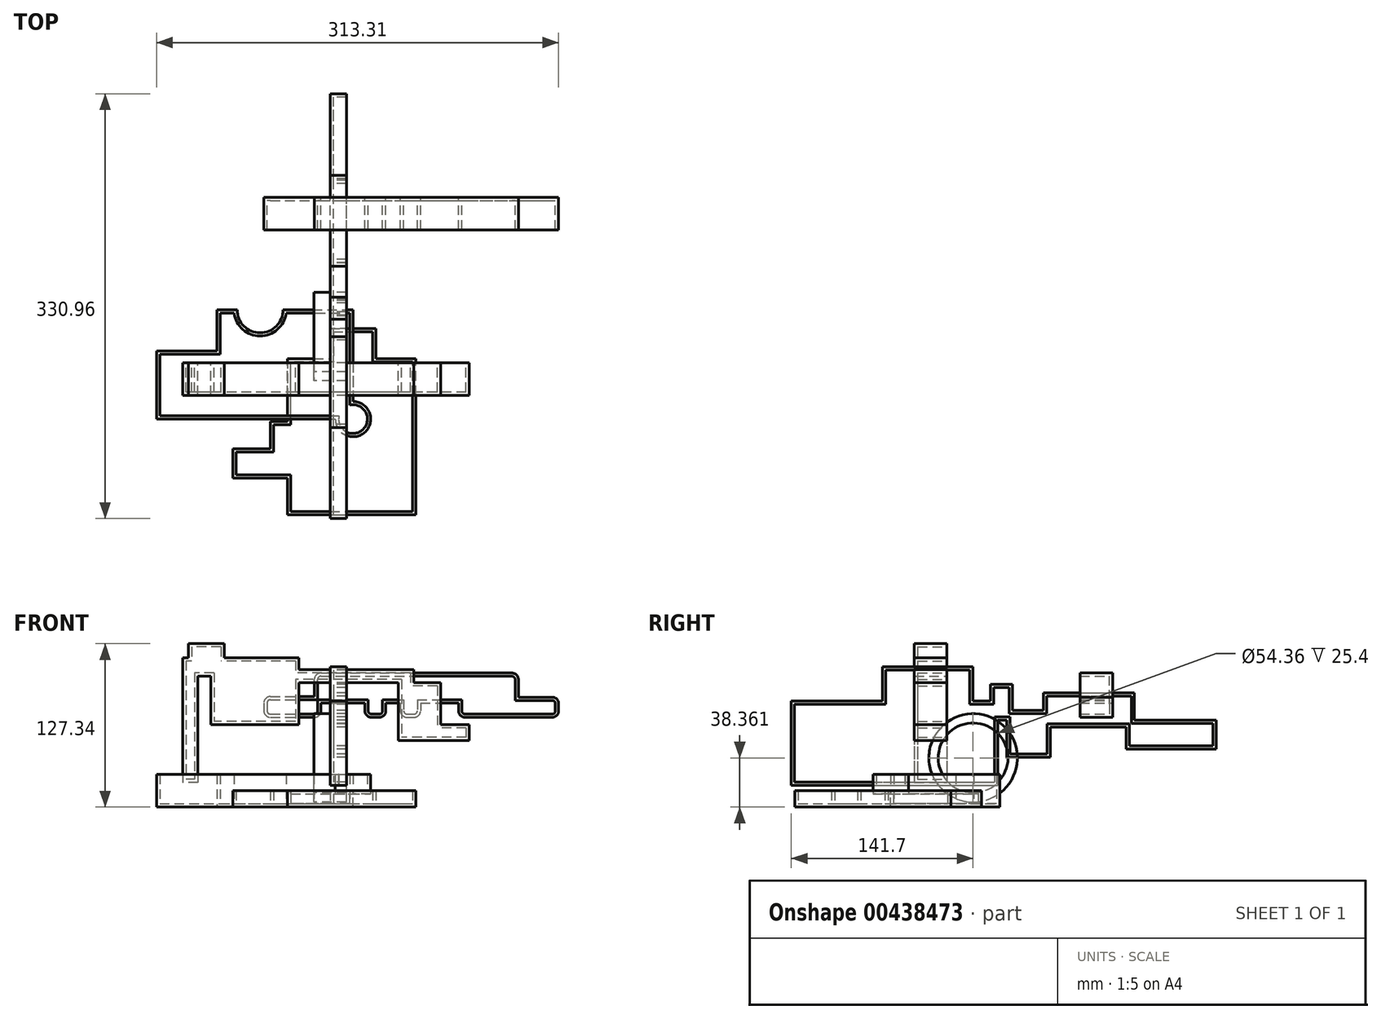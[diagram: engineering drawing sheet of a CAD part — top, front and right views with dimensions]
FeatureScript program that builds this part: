
annotation { "Feature Type Name" : "Feature", "Feature Type Description" : "" }
export const myFeature = defineFeature(function(context is Context, id is Id, definition is map)
    precondition{}
    {
        {
            var Q0;
            Q0=qCreatedBy(makeId("Top.planeOp"),FACE);
            var sketch = newSketch(context, id + "F0", { "sketchPlane" : qUnion([Q0])});
            skLineSegment(sketch, "E0.bottom", {"start": v(-135.25, -11) * mm, "end": v(17.85, -11) * mm});
            skLineSegment(sketch, "E0.top", {"start": v(-135.25, -64.2) * mm, "end": v(17.85, -64.2) * mm});
            skLineSegment(sketch, "E0.left", {"start": v(-135.25, -11) * mm, "end": v(-135.25, -64.2) * mm});
            skLineSegment(sketch, "E0.right", {"start": v(17.85, -11) * mm, "end": v(17.85, -64.2) * mm});
            skLineSegment(sketch, "E1.bottom", {"start": v(-88.25, -11) * mm, "end": v(17.85, -11) * mm});
            skLineSegment(sketch, "E1.top", {"start": v(-88.25, 20.9) * mm, "end": v(17.85, 20.9) * mm});
            skLineSegment(sketch, "E1.left", {"start": v(-88.25, -11) * mm, "end": v(-88.25, 20.9) * mm});
            skLineSegment(sketch, "E1.right", {"start": v(17.85, -11) * mm, "end": v(17.85, 20.9) * mm});
            skCircle(sketch, "E2", {"center": v(-54.53, 20.9) * mm, "radius": 17.86 * mm});
            skCircle(sketch, "E3", {"center": v(17.85, -64.2) * mm, "radius": 13.77 * mm});
            skSolve(sketch);
        }
        {
            var Q0;
            {var subQ0=sQuery(id+"F0.wireOp",EDGE,"E0.right");var subQ1=sQuery(id+"F0.wireOp",EDGE,"E0.top");var subQ2=makeQuery(id+"F0.imprint","INTERSECT",VERTEX,{"derivedFrom":[subQ1,subQ0]});Q0=makeQuery(id+"F0.imprint","IMPRINT",FACE,{"disambiguationData":[TD([[makeQuery(id+"F0.imprint","IMPRINT",EDGE,{"disambiguationData":[TD([[subQ2,1.0]])],"derivedFrom":subQ1}),-1.0]])]});}
            var Q1;
            {var subQ0=sQuery(id+"F0.wireOp",EDGE,"E2");var subQ1=sQuery(id+"F0.wireOp",EDGE,"E1.top");var subQ2=makeQuery(id+"F0.imprint","INTERSECT",VERTEX,{"disambiguationData":[OD(0.0)],"derivedFrom":[subQ1,subQ0]});Q1=makeQuery(id+"F0.imprint","IMPRINT",FACE,{"disambiguationData":[TD([[makeQuery(id+"F0.imprint","IMPRINT",EDGE,{"disambiguationData":[TD([[subQ2,-1.0]])],"derivedFrom":subQ1}),1.0]])]});}
            var Q2;
            {var subQ0=sQuery(id+"F0.wireOp",EDGE,"E0.right");var subQ1=sQuery(id+"F0.wireOp",EDGE,"E0.top");var subQ2=makeQuery(id+"F0.imprint","INTERSECT",VERTEX,{"derivedFrom":[subQ1,subQ0]});Q2=makeQuery(id+"F0.imprint","IMPRINT",FACE,{"disambiguationData":[TD([[makeQuery(id+"F0.imprint","IMPRINT",EDGE,{"disambiguationData":[TD([[subQ2,1.0]])],"derivedFrom":subQ1}),1.0]])]});}
            var Q3;
            Q3=makeQuery(id+"F0.imprint","IMPRINT",FACE,{"disambiguationData":[TD([[makeQuery(id+"F0.imprint","IMPRINT",EDGE,{"derivedFrom":sQuery(id+"F0.wireOp",EDGE,"E1.bottom")}),1.0]])]});
            var Q4;
            Q4=makeQuery(id+"F0.imprint","IMPRINT",FACE,{"disambiguationData":[TD([[makeQuery(id+"F0.imprint","IMPRINT",EDGE,{"derivedFrom":sQuery(id+"F0.wireOp",EDGE,"E0.bottom")}),-1.0]])]});
            var Q5;
            {var subQ0=sQuery(id+"F0.wireOp",EDGE,"E2");var subQ1=sQuery(id+"F0.wireOp",EDGE,"E1.top");var subQ2=makeQuery(id+"F0.imprint","INTERSECT",VERTEX,{"disambiguationData":[OD(0.0)],"derivedFrom":[subQ1,subQ0]});Q5=makeQuery(id+"F0.imprint","IMPRINT",FACE,{"disambiguationData":[TD([[makeQuery(id+"F0.imprint","IMPRINT",EDGE,{"disambiguationData":[TD([[subQ2,-1.0]])],"derivedFrom":subQ1}),-1.0]])]});}
            extrude(context, id + "F1", {"entities" : qUnion([Q0, Q1, Q2, Q3, Q4, Q5]), "depth" : 25.4 * mm});
        }
        {
            var Q0;
            Q0=makeQuery(id+"F1.opExtrude","CAP_FACE",FACE,{"disambiguationData":[OSD([sQuery(id+"F0.wireOp",EDGE,"E0.bottom"),sQuery(id+"F0.wireOp",EDGE,"E0.top"),sQuery(id+"F0.wireOp",EDGE,"E0.left"),sQuery(id+"F0.wireOp",EDGE,"E0.right"),sQuery(id+"F0.wireOp",EDGE,"E1.top"),sQuery(id+"F0.wireOp",EDGE,"E1.left"),sQuery(id+"F0.wireOp",EDGE,"E1.right"),sQuery(id+"F0.wireOp",EDGE,"E2"),sQuery(id+"F0.wireOp",EDGE,"E3")])],"isStart":false});
            shell(context, id + "F2", {"entities" : qUnion([Q0]), "thickness" : 2.54 * mm});
        }
        {
            var Q0;
            Q0=qCreatedBy(makeId("Top.planeOp"),FACE);
            var sketch = newSketch(context, id + "F3", { "sketchPlane" : qUnion([Q0])});
            skLineSegment(sketch, "E4.bottom", {"start": v(-33.13, -138.8) * mm, "end": v(66.9, -138.8) * mm});
            skLineSegment(sketch, "E4.top", {"start": v(-33.13, -17.16) * mm, "end": v(66.9, -17.16) * mm});
            skLineSegment(sketch, "E4.left", {"start": v(-33.13, -138.8) * mm, "end": v(-33.13, -17.16) * mm});
            skLineSegment(sketch, "E4.right", {"start": v(66.9, -138.8) * mm, "end": v(66.9, -17.16) * mm});
            skLineSegment(sketch, "E5.bottom", {"start": v(-75.86, -110.32) * mm, "end": v(0, -110.32) * mm});
            skLineSegment(sketch, "E5.top", {"start": v(-75.86, -87.33) * mm, "end": v(0, -87.33) * mm});
            skLineSegment(sketch, "E5.left", {"start": v(-75.86, -110.32) * mm, "end": v(-75.86, -87.33) * mm});
            skLineSegment(sketch, "E5.right", {"start": v(0, -110.32) * mm, "end": v(0, -87.33) * mm});
            skLineSegment(sketch, "E6.bottom", {"start": v(-46.46, -87.33) * mm, "end": v(-33.13, -87.33) * mm});
            skLineSegment(sketch, "E6.top", {"start": v(-46.46, -66.1) * mm, "end": v(-33.13, -66.1) * mm});
            skLineSegment(sketch, "E6.left", {"start": v(-46.46, -87.33) * mm, "end": v(-46.46, -66.1) * mm});
            skLineSegment(sketch, "E6.right", {"start": v(-33.13, -87.33) * mm, "end": v(-33.13, -66.1) * mm});
            skLineSegment(sketch, "E7.bottom", {"start": v(0, -20.29) * mm, "end": v(35.76, -20.29) * mm});
            skLineSegment(sketch, "E7.top", {"start": v(0, 6.47) * mm, "end": v(35.76, 6.47) * mm});
            skLineSegment(sketch, "E7.left", {"start": v(0, -20.29) * mm, "end": v(0, 6.47) * mm});
            skLineSegment(sketch, "E7.right", {"start": v(35.76, -20.29) * mm, "end": v(35.76, 6.47) * mm});
            skSolve(sketch);
        }
        {
            var Q0;
            Q0 = qSketchRegion(id + "F3", true);
            extrude(context, id + "F4", {"entities" : qUnion([Q0]), "operationType" : NewBodyOperationType.ADD, "depth" : 12.7 * mm});
        }
        {
            var Q0;
            {var subQ0=sQuery(id+"F3.wireOp",EDGE,"E5.bottom");var subQ1=sQuery(id+"F3.wireOp",EDGE,"E4.right");var subQ2=sQuery(id+"F3.wireOp",EDGE,"E4.left");var subQ3=sQuery(id+"F3.wireOp",EDGE,"E4.top");var subQ4=sQuery(id+"F3.wireOp",EDGE,"E6.top");var subQ5=sQuery(id+"F3.wireOp",EDGE,"E7.right");var subQ6=sQuery(id+"F3.wireOp",EDGE,"E5.top");var subQ7=sQuery(id+"F3.wireOp",EDGE,"E7.top");var subQ8=sQuery(id+"F3.wireOp",EDGE,"E4.bottom");var subQ9=sQuery(id+"F3.wireOp",EDGE,"E5.left");var subQ10=sQuery(id+"F3.wireOp",EDGE,"E6.left");Q0=makeQuery(id+"F4.boolean.opBoolean","SPLIT",FACE,{"disambiguationData":[TD([makeQuery(id+"F1.opExtrude","SWEPT_FACE",FACE,{"disambiguationData":[OSD([sQuery(id+"F0.wireOp",EDGE,"E0.top")])]})])],"derivedFrom":makeQuery(id+"F4.opExtrude","CAP_FACE",FACE,{"disambiguationData":[OSD([subQ8,subQ3,subQ2,subQ1,subQ0,subQ6,subQ9,subQ4,subQ10,subQ7,sQuery(id+"F3.wireOp",EDGE,"E7.left"),subQ5])],"isStart":false})});}
            shell(context, id + "F5", {"entities" : qUnion([Q0]), "thickness" : 2.54 * mm});
        }
        {
            var Q0;
            Q0=qCreatedBy(makeId("Front.planeOp"),FACE);
            var sketch = newSketch(context, id + "F6", { "sketchPlane" : qUnion([Q0])});
            skLineSegment(sketch, "E8.bottom", {"start": v(-51.64, 86.18) * mm, "end": v(-7.14, 86.18) * mm});
            skLineSegment(sketch, "E8.top", {"start": v(-51.64, 69.95) * mm, "end": v(-7.14, 69.95) * mm});
            skLineSegment(sketch, "E8.left", {"start": v(-51.64, 86.18) * mm, "end": v(-51.64, 69.95) * mm});
            skLineSegment(sketch, "E8.right", {"start": v(-7.14, 86.18) * mm, "end": v(-7.14, 69.95) * mm});
            skLineSegment(sketch, "E9.bottom", {"start": v(-12.3, 81.04) * mm, "end": v(146.7, 81.04) * mm});
            skLineSegment(sketch, "E9.top", {"start": v(-12.3, 104.47) * mm, "end": v(146.7, 104.47) * mm});
            skLineSegment(sketch, "E9.left", {"start": v(-12.3, 81.04) * mm, "end": v(-12.3, 104.47) * mm});
            skLineSegment(sketch, "E9.right", {"start": v(146.7, 81.04) * mm, "end": v(146.7, 104.47) * mm});
            skLineSegment(sketch, "E10.bottom", {"start": v(27.15, 86.87) * mm, "end": v(43.44, 86.87) * mm});
            skLineSegment(sketch, "E10.top", {"start": v(27.15, 69.95) * mm, "end": v(43.44, 69.95) * mm});
            skLineSegment(sketch, "E10.left", {"start": v(27.15, 86.87) * mm, "end": v(27.15, 69.95) * mm});
            skLineSegment(sketch, "E10.right", {"start": v(43.44, 86.87) * mm, "end": v(43.44, 69.95) * mm});
            skLineSegment(sketch, "E11.bottom", {"start": v(54.8, 87.86) * mm, "end": v(70.48, 87.86) * mm});
            skLineSegment(sketch, "E11.top", {"start": v(54.8, 69.95) * mm, "end": v(70.48, 69.95) * mm});
            skLineSegment(sketch, "E11.left", {"start": v(54.8, 87.86) * mm, "end": v(54.8, 69.95) * mm});
            skLineSegment(sketch, "E11.right", {"start": v(70.48, 87.86) * mm, "end": v(70.48, 69.95) * mm});
            skLineSegment(sketch, "E12.bottom", {"start": v(100.04, 85.67) * mm, "end": v(178.06, 85.67) * mm});
            skLineSegment(sketch, "E12.top", {"start": v(100.04, 69.95) * mm, "end": v(178.06, 69.95) * mm});
            skLineSegment(sketch, "E12.left", {"start": v(100.04, 85.67) * mm, "end": v(100.04, 69.95) * mm});
            skLineSegment(sketch, "E12.right", {"start": v(178.06, 85.67) * mm, "end": v(178.06, 69.95) * mm});
            skSolve(sketch);
        }
        {
            var Q0;
            Q0 = qSketchRegion(id + "F6", true);
            extrude(context, id + "F7", {"entities" : qUnion([Q0]), "depth" : 25.4 * mm});
        }
        {
            var Q0;
            Q0=makeQuery(id+"F7.opExtrude","SWEPT_EDGE",EDGE,{"disambiguationData":[OSD([sQuery(id+"F6.wireOp",EDGE,"E9.top"),sQuery(id+"F6.wireOp",EDGE,"E9.right")])]});
            var Q1;
            Q1=makeQuery(id+"F7.opExtrude","SWEPT_EDGE",EDGE,{"disambiguationData":[OSD([sQuery(id+"F6.wireOp",EDGE,"E12.bottom"),sQuery(id+"F6.wireOp",EDGE,"E12.right")])]});
            var Q2;
            Q2=makeQuery(id+"F7.opExtrude","SWEPT_EDGE",EDGE,{"disambiguationData":[OSD([sQuery(id+"F6.wireOp",EDGE,"E9.top"),sQuery(id+"F6.wireOp",EDGE,"E9.left")])]});
            var Q3;
            Q3=makeQuery(id+"F7.opExtrude","SWEPT_EDGE",EDGE,{"disambiguationData":[OSD([sQuery(id+"F6.wireOp",EDGE,"E8.bottom"),sQuery(id+"F6.wireOp",EDGE,"E8.left")])]});
            var Q4;
            Q4=makeQuery(id+"F7.opExtrude","SWEPT_EDGE",EDGE,{"disambiguationData":[OSD([sQuery(id+"F6.wireOp",EDGE,"E8.top"),sQuery(id+"F6.wireOp",EDGE,"E8.left")])]});
            var Q5;
            Q5=makeQuery(id+"F7.opExtrude","SWEPT_EDGE",EDGE,{"disambiguationData":[OSD([sQuery(id+"F6.wireOp",EDGE,"E12.top"),sQuery(id+"F6.wireOp",EDGE,"E12.left")])]});
            var Q6;
            Q6=makeQuery(id+"F7.opExtrude","SWEPT_EDGE",EDGE,{"disambiguationData":[OSD([sQuery(id+"F6.wireOp",EDGE,"E11.top"),sQuery(id+"F6.wireOp",EDGE,"E11.left")])]});
            var Q7;
            Q7=makeQuery(id+"F7.opExtrude","SWEPT_EDGE",EDGE,{"disambiguationData":[OSD([sQuery(id+"F6.wireOp",EDGE,"E10.top"),sQuery(id+"F6.wireOp",EDGE,"E10.left")])]});
            var Q8;
            Q8=makeQuery(id+"F7.opExtrude","SWEPT_EDGE",EDGE,{"disambiguationData":[OSD([sQuery(id+"F6.wireOp",EDGE,"E12.top"),sQuery(id+"F6.wireOp",EDGE,"E12.right")])]});
            var Q9;
            Q9=makeQuery(id+"F7.opExtrude","SWEPT_EDGE",EDGE,{"disambiguationData":[OSD([sQuery(id+"F6.wireOp",EDGE,"E8.top"),sQuery(id+"F6.wireOp",EDGE,"E8.right")])]});
            var Q10;
            Q10=makeQuery(id+"F7.opExtrude","SWEPT_EDGE",EDGE,{"disambiguationData":[OSD([sQuery(id+"F6.wireOp",EDGE,"E11.top"),sQuery(id+"F6.wireOp",EDGE,"E11.right")])]});
            var Q11;
            Q11=makeQuery(id+"F7.opExtrude","SWEPT_EDGE",EDGE,{"disambiguationData":[OSD([sQuery(id+"F6.wireOp",EDGE,"E10.top"),sQuery(id+"F6.wireOp",EDGE,"E10.right")])]});
            fillet(context, id + "F8", {"entities" : qUnion([Q0, Q1, Q2, Q3, Q4, Q5, Q6, Q7, Q8, Q9, Q10, Q11]), "radius" : 5.08 * mm, "tangentPropagation" : true, "allowEdgeOverflow" : false});
        }
        {
            var Q0;
            Q0=qCreatedBy(makeId("Right.planeOp"),FACE);
            var sketch = newSketch(context, id + "F9", { "sketchPlane" : qUnion([Q0])});
            skLineSegment(sketch, "E13.bottom", {"start": v(-141.7, 82.81) * mm, "end": v(19.28, 82.81) * mm});
            skLineSegment(sketch, "E13.top", {"start": v(-141.7, 17.06) * mm, "end": v(19.28, 17.06) * mm});
            skLineSegment(sketch, "E13.left", {"start": v(-141.7, 82.81) * mm, "end": v(-141.7, 17.06) * mm});
            skLineSegment(sketch, "E13.right", {"start": v(19.28, 82.81) * mm, "end": v(19.28, 17.06) * mm});
            skLineSegment(sketch, "E14.bottom", {"start": v(-70.73, 109.28) * mm, "end": v(0, 109.28) * mm});
            skLineSegment(sketch, "E14.top", {"start": v(-70.73, 58.4) * mm, "end": v(0, 58.4) * mm});
            skLineSegment(sketch, "E14.left", {"start": v(-70.73, 109.28) * mm, "end": v(-70.73, 58.4) * mm});
            skLineSegment(sketch, "E14.right", {"start": v(0, 109.28) * mm, "end": v(0, 58.4) * mm});
            skLineSegment(sketch, "E15.bottom", {"start": v(13.48, 95.63) * mm, "end": v(30.68, 95.63) * mm});
            skLineSegment(sketch, "E15.top", {"start": v(13.48, 67.67) * mm, "end": v(30.68, 67.67) * mm});
            skLineSegment(sketch, "E15.left", {"start": v(13.48, 95.63) * mm, "end": v(13.48, 67.67) * mm});
            skLineSegment(sketch, "E15.right", {"start": v(30.68, 95.63) * mm, "end": v(30.68, 67.67) * mm});
            skLineSegment(sketch, "E16.bottom", {"start": v(26.26, 75.35) * mm, "end": v(60.2, 75.35) * mm});
            skLineSegment(sketch, "E16.top", {"start": v(26.26, 38.94) * mm, "end": v(60.2, 38.94) * mm});
            skLineSegment(sketch, "E16.left", {"start": v(26.26, 75.35) * mm, "end": v(26.26, 38.94) * mm});
            skLineSegment(sketch, "E16.right", {"start": v(60.2, 75.35) * mm, "end": v(60.2, 38.94) * mm});
            skLineSegment(sketch, "E17.bottom", {"start": v(54.85, 88.97) * mm, "end": v(125.74, 88.97) * mm});
            skLineSegment(sketch, "E17.top", {"start": v(54.85, 62.28) * mm, "end": v(125.74, 62.28) * mm});
            skLineSegment(sketch, "E17.left", {"start": v(54.85, 88.97) * mm, "end": v(54.85, 62.28) * mm});
            skLineSegment(sketch, "E17.right", {"start": v(125.74, 88.97) * mm, "end": v(125.74, 62.28) * mm});
            skLineSegment(sketch, "E18.bottom", {"start": v(119.35, 67.67) * mm, "end": v(189.26, 67.67) * mm});
            skLineSegment(sketch, "E18.top", {"start": v(119.35, 45.27) * mm, "end": v(189.26, 45.27) * mm});
            skLineSegment(sketch, "E18.left", {"start": v(119.35, 67.67) * mm, "end": v(119.35, 45.27) * mm});
            skLineSegment(sketch, "E18.right", {"start": v(189.26, 67.67) * mm, "end": v(189.26, 45.27) * mm});
            skSolve(sketch);
        }
        {
            var Q0;
            Q0 = qSketchRegion(id + "F9", true);
            extrude(context, id + "F10", {"entities" : qUnion([Q0]), "depth" : 12.7 * mm});
        }
        {
            var Q0;
            Q0=makeQuery(id+"F10.opExtrude","CAP_FACE",FACE,{"disambiguationData":[OSD([sQuery(id+"F9.wireOp",EDGE,"E13.bottom"),sQuery(id+"F9.wireOp",EDGE,"E13.top"),sQuery(id+"F9.wireOp",EDGE,"E13.left"),sQuery(id+"F9.wireOp",EDGE,"E13.right"),sQuery(id+"F9.wireOp",EDGE,"E14.bottom"),sQuery(id+"F9.wireOp",EDGE,"E14.left"),sQuery(id+"F9.wireOp",EDGE,"E14.right"),sQuery(id+"F9.wireOp",EDGE,"E15.bottom"),sQuery(id+"F9.wireOp",EDGE,"E15.top"),sQuery(id+"F9.wireOp",EDGE,"E15.left"),sQuery(id+"F9.wireOp",EDGE,"E15.right"),sQuery(id+"F9.wireOp",EDGE,"E16.bottom"),sQuery(id+"F9.wireOp",EDGE,"E16.top"),sQuery(id+"F9.wireOp",EDGE,"E16.left"),sQuery(id+"F9.wireOp",EDGE,"E16.right"),sQuery(id+"F9.wireOp",EDGE,"E17.bottom"),sQuery(id+"F9.wireOp",EDGE,"E17.top"),sQuery(id+"F9.wireOp",EDGE,"E17.left"),sQuery(id+"F9.wireOp",EDGE,"E17.right"),sQuery(id+"F9.wireOp",EDGE,"E18.bottom"),sQuery(id+"F9.wireOp",EDGE,"E18.top"),sQuery(id+"F9.wireOp",EDGE,"E18.left"),sQuery(id+"F9.wireOp",EDGE,"E18.right")])],"isStart":false});
            var Q1;
            Q1=makeQuery(id+"F7.opExtrude","CAP_FACE",FACE,{"disambiguationData":[OSD([sQuery(id+"F6.wireOp",EDGE,"E8.bottom"),sQuery(id+"F6.wireOp",EDGE,"E8.top"),sQuery(id+"F6.wireOp",EDGE,"E8.left"),sQuery(id+"F6.wireOp",EDGE,"E8.right"),sQuery(id+"F6.wireOp",EDGE,"E9.bottom"),sQuery(id+"F6.wireOp",EDGE,"E9.top"),sQuery(id+"F6.wireOp",EDGE,"E9.left"),sQuery(id+"F6.wireOp",EDGE,"E9.right"),sQuery(id+"F6.wireOp",EDGE,"E10.top"),sQuery(id+"F6.wireOp",EDGE,"E10.left"),sQuery(id+"F6.wireOp",EDGE,"E10.right"),sQuery(id+"F6.wireOp",EDGE,"E11.top"),sQuery(id+"F6.wireOp",EDGE,"E11.left"),sQuery(id+"F6.wireOp",EDGE,"E11.right"),sQuery(id+"F6.wireOp",EDGE,"E12.bottom"),sQuery(id+"F6.wireOp",EDGE,"E12.top"),sQuery(id+"F6.wireOp",EDGE,"E12.left"),sQuery(id+"F6.wireOp",EDGE,"E12.right")])],"isStart":false});
            shell(context, id + "F11", {"entities" : qUnion([Q0, Q1]), "thickness" : 2.54 * mm});
        }
        {
            var Q0;
            Q0=makeQuery(id+"F7.opExtrude","SWEPT_BODY",BODY,{"disambiguationData":[OSD([sQuery(id+"F6.wireOp",EDGE,"E8.bottom"),sQuery(id+"F6.wireOp",EDGE,"E8.top"),sQuery(id+"F6.wireOp",EDGE,"E8.left"),sQuery(id+"F6.wireOp",EDGE,"E8.right"),sQuery(id+"F6.wireOp",EDGE,"E9.bottom"),sQuery(id+"F6.wireOp",EDGE,"E9.top"),sQuery(id+"F6.wireOp",EDGE,"E9.left"),sQuery(id+"F6.wireOp",EDGE,"E9.right"),sQuery(id+"F6.wireOp",EDGE,"E10.top"),sQuery(id+"F6.wireOp",EDGE,"E10.left"),sQuery(id+"F6.wireOp",EDGE,"E10.right"),sQuery(id+"F6.wireOp",EDGE,"E11.top"),sQuery(id+"F6.wireOp",EDGE,"E11.left"),sQuery(id+"F6.wireOp",EDGE,"E11.right"),sQuery(id+"F6.wireOp",EDGE,"E12.bottom"),sQuery(id+"F6.wireOp",EDGE,"E12.top"),sQuery(id+"F6.wireOp",EDGE,"E12.left"),sQuery(id+"F6.wireOp",EDGE,"E12.right")])]});
            transform(context, id + "F12", {"entities" : qUnion([Q0]), "transformType" : TransformType.TRANSLATION_3D, "dx" : 0 * mm, "dy" : 108.7 * mm, "dz" : 0 * mm, "makeCopy" : false});
        }
        {
            var Q0;
            Q0=qCreatedBy(makeId("Right.planeOp"),FACE);
            var sketch = newSketch(context, id + "F13", { "sketchPlane" : qUnion([Q0])});
            skCircle(sketch, "E19", {"center": v(-26.54, 13.88) * mm, "radius": 31.15 * mm});
            skPoint(sketch, "E19.first.point", {"position": v(-4.11, 35.5) * mm});
            skPoint(sketch, "E19.second.point", {"position": v(-57.32, 9.12) * mm});
            skPoint(sketch, "E19.third.point", {"position": v(-19, 44.1) * mm});
            skSolve(sketch);
        }
        {
            var Q0;
            Q0=qCreatedBy(makeId("Right.planeOp"),FACE);
            var sketch = newSketch(context, id + "F14", { "sketchPlane" : qUnion([Q0])});
            skCircle(sketch, "E20", {"center": v(0, 38.36) * mm, "radius": 34.45 * mm});
            skCircle(sketch, "E21", {"center": v(0, 38.36) * mm, "radius": 27.18 * mm});
            skSolve(sketch);
        }
        {
            var Q0;
            Q0=makeQuery(id+"F14.imprint","IMPRINT",FACE,{"disambiguationData":[TD([[makeQuery(id+"F14.imprint","IMPRINT",EDGE,{"derivedFrom":sQuery(id+"F14.wireOp",EDGE,"E20")}),1.0]])]});
            extrude(context, id + "F15", {"entities" : qUnion([Q0]), "endBound" : BoundingType.SYMMETRIC, "depth" : 25.4 * mm});
        }
        {
            var Q0;
            Q0=qCreatedBy(makeId("Front.planeOp"),FACE);
            var sketch = newSketch(context, id + "F16", { "sketchPlane" : qUnion([Q0])});
            skLineSegment(sketch, "E22.bottom", {"start": v(108.5, 64.38) * mm, "end": v(53.24, 64.38) * mm});
            skLineSegment(sketch, "E22.top", {"start": v(108.5, 51.79) * mm, "end": v(53.24, 51.79) * mm});
            skLineSegment(sketch, "E22.left", {"start": v(108.5, 64.38) * mm, "end": v(108.5, 51.79) * mm});
            skLineSegment(sketch, "E22.right", {"start": v(53.24, 64.38) * mm, "end": v(53.24, 51.79) * mm});
            skLineSegment(sketch, "E23.bottom", {"start": v(86.12, 96.85) * mm, "end": v(53.24, 96.85) * mm});
            skLineSegment(sketch, "E23.top", {"start": v(86.12, 58.08) * mm, "end": v(53.24, 58.08) * mm});
            skLineSegment(sketch, "E23.left", {"start": v(86.12, 96.85) * mm, "end": v(86.12, 58.08) * mm});
            skLineSegment(sketch, "E23.right", {"start": v(53.24, 96.85) * mm, "end": v(53.24, 58.08) * mm});
            skPoint(sketch, "E24.oppositeSnap0", {"position": v(69.68, 96.85) * mm});
            skLineSegment(sketch, "E24.bottom", {"start": v(65.13, 106.96) * mm, "end": v(-34.42, 106.96) * mm});
            skLineSegment(sketch, "E24.top", {"start": v(65.13, 96.85) * mm, "end": v(-34.42, 96.85) * mm});
            skLineSegment(sketch, "E24.left", {"start": v(65.13, 106.96) * mm, "end": v(65.13, 96.85) * mm});
            skLineSegment(sketch, "E24.right", {"start": v(-34.42, 106.96) * mm, "end": v(-34.42, 96.85) * mm});
            skLineSegment(sketch, "E25.bottom", {"start": v(-24.48, 116.39) * mm, "end": v(-92.88, 116.39) * mm});
            skLineSegment(sketch, "E25.top", {"start": v(-24.48, 64.38) * mm, "end": v(-92.88, 64.38) * mm});
            skLineSegment(sketch, "E25.left", {"start": v(-24.48, 116.39) * mm, "end": v(-24.48, 64.38) * mm});
            skLineSegment(sketch, "E25.right", {"start": v(-92.88, 116.39) * mm, "end": v(-92.88, 64.38) * mm});
            skLineSegment(sketch, "E26.bottom", {"start": v(-82.51, 127.34) * mm, "end": v(-110.4, 127.34) * mm});
            skLineSegment(sketch, "E26.top", {"start": v(-82.51, 102.13) * mm, "end": v(-110.4, 102.13) * mm});
            skLineSegment(sketch, "E26.left", {"start": v(-82.51, 127.34) * mm, "end": v(-82.51, 102.13) * mm});
            skLineSegment(sketch, "E26.right", {"start": v(-110.4, 127.34) * mm, "end": v(-110.4, 102.13) * mm});
            skLineSegment(sketch, "E27.bottom", {"start": v(-103, 116.39) * mm, "end": v(-114.91, 116.39) * mm});
            skLineSegment(sketch, "E27.top", {"start": v(-103, 19.24) * mm, "end": v(-114.91, 19.24) * mm});
            skLineSegment(sketch, "E27.left", {"start": v(-103, 116.39) * mm, "end": v(-103, 19.24) * mm});
            skLineSegment(sketch, "E27.right", {"start": v(-114.91, 116.39) * mm, "end": v(-114.91, 19.24) * mm});
            skSolve(sketch);
        }
        {
            var Q0;
            Q0 = qSketchRegion(id + "F16", true);
            extrude(context, id + "F17", {"entities" : qUnion([Q0]), "depth" : 25.4 * mm});
        }
        {
            var Q0;
            Q0=makeQuery(id+"F17.opExtrude","SWEPT_BODY",BODY,{"disambiguationData":[OSD([sQuery(id+"F16.wireOp",EDGE,"E22.bottom"),sQuery(id+"F16.wireOp",EDGE,"E22.top"),sQuery(id+"F16.wireOp",EDGE,"E22.left"),sQuery(id+"F16.wireOp",EDGE,"E22.right"),sQuery(id+"F16.wireOp",EDGE,"E23.bottom"),sQuery(id+"F16.wireOp",EDGE,"E23.left"),sQuery(id+"F16.wireOp",EDGE,"E23.right"),sQuery(id+"F16.wireOp",EDGE,"E24.bottom"),sQuery(id+"F16.wireOp",EDGE,"E24.top"),sQuery(id+"F16.wireOp",EDGE,"E24.left"),sQuery(id+"F16.wireOp",EDGE,"E25.bottom"),sQuery(id+"F16.wireOp",EDGE,"E25.top"),sQuery(id+"F16.wireOp",EDGE,"E25.left"),sQuery(id+"F16.wireOp",EDGE,"E25.right"),sQuery(id+"F16.wireOp",EDGE,"E26.bottom"),sQuery(id+"F16.wireOp",EDGE,"E26.top"),sQuery(id+"F16.wireOp",EDGE,"E26.left"),sQuery(id+"F16.wireOp",EDGE,"E26.right"),sQuery(id+"F16.wireOp",EDGE,"E27.bottom"),sQuery(id+"F16.wireOp",EDGE,"E27.top"),sQuery(id+"F16.wireOp",EDGE,"E27.left"),sQuery(id+"F16.wireOp",EDGE,"E27.right")])]});
            transform(context, id + "F18", {"entities" : qUnion([Q0]), "transformType" : TransformType.TRANSLATION_3D, "dx" : 0 * mm, "dy" : -20.32 * mm, "dz" : 0 * mm, "makeCopy" : false});
        }
        {
            var Q0;
            Q0=makeQuery(id+"F17.opExtrude","CAP_FACE",FACE,{"disambiguationData":[OSD([sQuery(id+"F16.wireOp",EDGE,"E22.bottom"),sQuery(id+"F16.wireOp",EDGE,"E22.top"),sQuery(id+"F16.wireOp",EDGE,"E22.left"),sQuery(id+"F16.wireOp",EDGE,"E22.right"),sQuery(id+"F16.wireOp",EDGE,"E23.bottom"),sQuery(id+"F16.wireOp",EDGE,"E23.left"),sQuery(id+"F16.wireOp",EDGE,"E23.right"),sQuery(id+"F16.wireOp",EDGE,"E24.bottom"),sQuery(id+"F16.wireOp",EDGE,"E24.top"),sQuery(id+"F16.wireOp",EDGE,"E24.left"),sQuery(id+"F16.wireOp",EDGE,"E25.bottom"),sQuery(id+"F16.wireOp",EDGE,"E25.top"),sQuery(id+"F16.wireOp",EDGE,"E25.left"),sQuery(id+"F16.wireOp",EDGE,"E25.right"),sQuery(id+"F16.wireOp",EDGE,"E26.bottom"),sQuery(id+"F16.wireOp",EDGE,"E26.top"),sQuery(id+"F16.wireOp",EDGE,"E26.left"),sQuery(id+"F16.wireOp",EDGE,"E26.right"),sQuery(id+"F16.wireOp",EDGE,"E27.bottom"),sQuery(id+"F16.wireOp",EDGE,"E27.top"),sQuery(id+"F16.wireOp",EDGE,"E27.left"),sQuery(id+"F16.wireOp",EDGE,"E27.right")])],"isStart":true});
            shell(context, id + "F19", {"entities" : qUnion([Q0]), "thickness" : 2.54 * mm});
        }
    });
